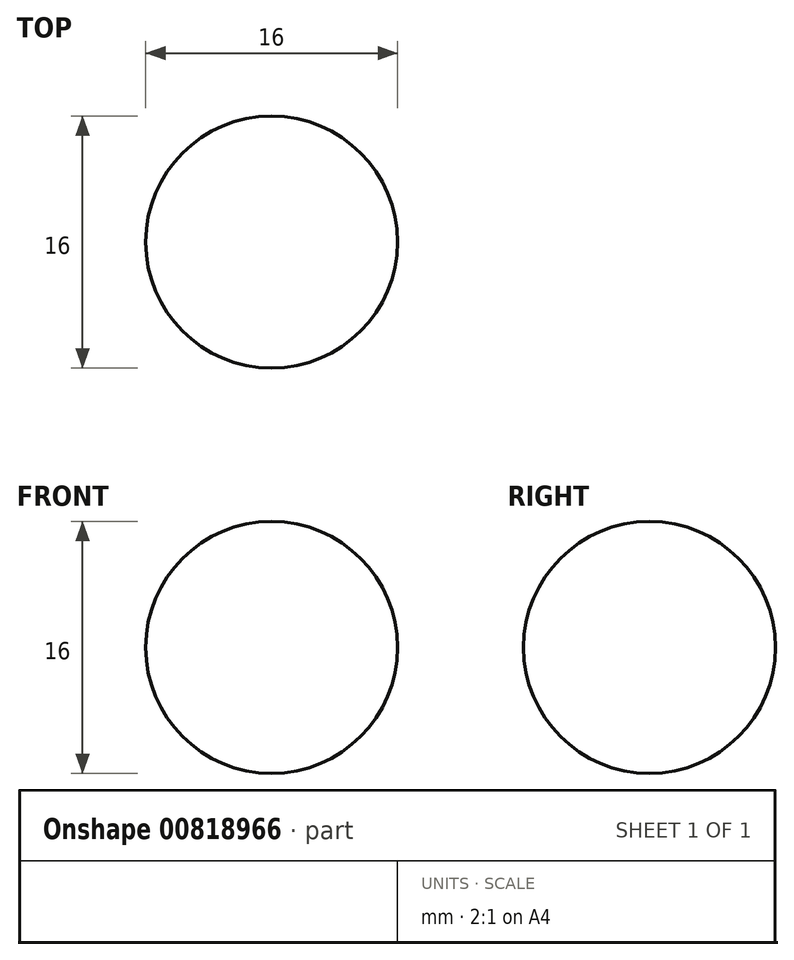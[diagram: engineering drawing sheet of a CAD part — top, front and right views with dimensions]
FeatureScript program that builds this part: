
annotation { "Feature Type Name" : "Feature", "Feature Type Description" : "" }
export const myFeature = defineFeature(function(context is Context, id is Id, definition is map)
    precondition{}
    {
        {
            var Q0;
            Q0=qCreatedBy(makeId("Right.planeOp"),FACE);
            var sketch = newSketch(context, id + "F0", { "sketchPlane" : qUnion([Q0])});
            skArc(sketch, "E0", {"start": v(0, -8) * mm, "mid": v(8, 0) * mm, "end": v(0, 8) * mm});
            skLineSegment(sketch, "E1", {"start": v(0, -19.02) * mm, "end": v(0, 28.7) * mm, "construction": true});
            skSolve(sketch);
        }
        {
            var Q0;
            Q0=sQuery(id+"F0.wireOp",EDGE,"E0");
            var Q1;
            Q1=sQuery(id+"F0.wireOp",EDGE,"E1");
            revolve(context, id + "F1", {"bodyType" : ToolBodyType.SURFACE, "surfaceOperationType" : NewSurfaceOperationType.NEW, "surfaceEntities" : qUnion([Q0]), "axis" : qUnion([Q1]), "revolveType" : RevolveType.FULL});
        }
    });
